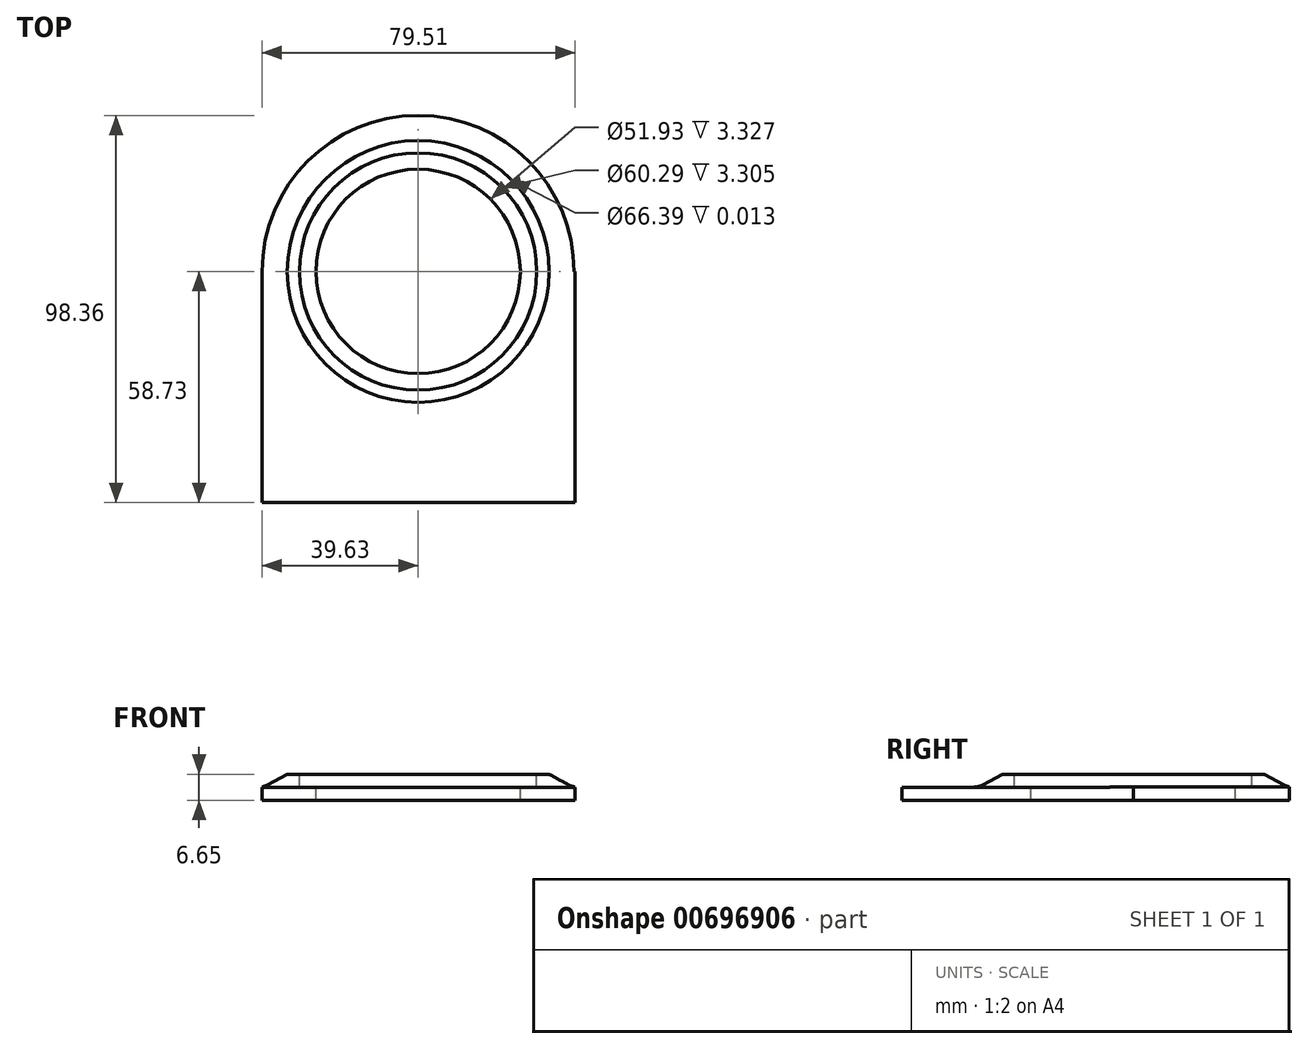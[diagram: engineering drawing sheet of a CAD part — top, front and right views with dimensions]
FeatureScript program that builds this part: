
annotation { "Feature Type Name" : "Feature", "Feature Type Description" : "" }
export const myFeature = defineFeature(function(context is Context, id is Id, definition is map)
    precondition{}
    {
        {
            var Q0;
            Q0=qCreatedBy(makeId("Top.planeOp"),FACE);
            var sketch = newSketch(context, id + "F0", { "sketchPlane" : qUnion([Q0])});
            skCircle(sketch, "E0", {"center": v(0, 0) * mm, "radius": 30.21 * mm});
            skCircle(sketch, "E1", {"center": v(0, 0) * mm, "radius": 26.11 * mm});
            skCircle(sketch, "E2", {"center": v(0, 0) * mm, "radius": 33.2 * mm});
            skCircle(sketch, "E3", {"center": v(0, 0) * mm, "radius": 39.63 * mm});
            skLineSegment(sketch, "E4.bottom", {"start": v(-39.63, 0) * mm, "end": v(39.88, 0) * mm});
            skLineSegment(sketch, "E4.top", {"start": v(-39.63, -58.73) * mm, "end": v(39.88, -58.73) * mm});
            skLineSegment(sketch, "E4.left", {"start": v(-39.63, 0) * mm, "end": v(-39.63, -58.73) * mm});
            skLineSegment(sketch, "E4.right", {"start": v(39.88, 0) * mm, "end": v(39.88, -58.73) * mm});
            skSolve(sketch);
        }
        {
            var Q0;
            Q0=qCreatedBy(makeId("Front.planeOp"),FACE);
            var sketch = newSketch(context, id + "F1", { "sketchPlane" : qUnion([Q0])});
            skLineSegment(sketch, "E5.bottom", {"start": v(39.37, -4.97) * mm, "end": v(-39.37, -4.97) * mm});
            skLineSegment(sketch, "E5.top", {"start": v(39.37, 4.97) * mm, "end": v(-39.37, 4.97) * mm});
            skLineSegment(sketch, "E5.left", {"start": v(39.37, -4.97) * mm, "end": v(39.37, 4.97) * mm});
            skLineSegment(sketch, "E5.right", {"start": v(-39.37, -4.97) * mm, "end": v(-39.37, 4.97) * mm});
            skPoint(sketch, "E5.middle", {"position": v(0, 0) * mm});
            skLineSegment(sketch, "E6.bottom", {"start": v(33.25, -4.97) * mm, "end": v(-33.25, -4.97) * mm});
            skLineSegment(sketch, "E6.top", {"start": v(33.25, 4.97) * mm, "end": v(-33.25, 4.97) * mm});
            skLineSegment(sketch, "E6.left", {"start": v(33.25, -4.97) * mm, "end": v(33.25, 4.97) * mm});
            skLineSegment(sketch, "E6.right", {"start": v(-33.25, -4.97) * mm, "end": v(-33.25, 4.97) * mm});
            skLineSegment(sketch, "E7.bottom", {"start": v(25.97, -4.97) * mm, "end": v(-25.97, -4.97) * mm});
            skLineSegment(sketch, "E7.top", {"start": v(25.97, 4.97) * mm, "end": v(-25.97, 4.97) * mm});
            skLineSegment(sketch, "E7.left", {"start": v(25.97, -4.97) * mm, "end": v(25.97, 4.97) * mm});
            skLineSegment(sketch, "E7.right", {"start": v(-25.97, -4.97) * mm, "end": v(-25.97, 4.97) * mm});
            skLineSegment(sketch, "E8.bottom", {"start": v(30.15, -4.97) * mm, "end": v(-30.15, -4.97) * mm});
            skLineSegment(sketch, "E8.top", {"start": v(30.15, 4.97) * mm, "end": v(-30.15, 4.97) * mm});
            skLineSegment(sketch, "E8.left", {"start": v(30.15, -4.97) * mm, "end": v(30.15, 4.97) * mm});
            skLineSegment(sketch, "E8.right", {"start": v(-30.15, -4.97) * mm, "end": v(-30.15, 4.97) * mm});
            skLineSegment(sketch, "E9.bottom", {"start": v(39.37, -1.66) * mm, "end": v(-39.37, -1.66) * mm});
            skLineSegment(sketch, "E9.top", {"start": v(39.37, 1.66) * mm, "end": v(-39.37, 1.66) * mm});
            skLineSegment(sketch, "E9.left", {"start": v(39.37, -1.66) * mm, "end": v(39.37, 1.66) * mm});
            skLineSegment(sketch, "E9.right", {"start": v(-39.37, -1.66) * mm, "end": v(-39.37, 1.66) * mm});
            skLineSegment(sketch, "E10", {"start": v(-39.37, 1.66) * mm, "end": v(-33.25, 4.97) * mm});
            skLineSegment(sketch, "E11", {"start": v(33.25, 4.97) * mm, "end": v(39.37, 1.66) * mm});
            skLineSegment(sketch, "E12", {"start": v(0, 4.97) * mm, "end": v(0, -4.97) * mm});
            skSolve(sketch);
        }
        {
            var Q0;
            {var subQ0=sQuery(id+"F1.wireOp",EDGE,"E10");Q0=makeQuery(id+"F1.imprint","IMPRINT",FACE,{"disambiguationData":[TD([[makeQuery(id+"F1.imprint","IMPRINT",EDGE,{"derivedFrom":subQ0}),-1.0]])]});}
            var Q1;
            {var subQ0=sQuery(id+"F1.wireOp",EDGE,"E6.right");var subQ5=sQuery(id+"F1.wireOp",EDGE,"E9.top");var subQ6=makeQuery(id+"F1.imprint","INTERSECT",VERTEX,{"derivedFrom":[subQ0,subQ5]});Q1=makeQuery(id+"F1.imprint","IMPRINT",FACE,{"disambiguationData":[TD([[makeQuery(id+"F1.imprint","IMPRINT",EDGE,{"disambiguationData":[TD([[subQ6,1.0]])],"derivedFrom":subQ5}),-1.0]])]});}
            var Q2;
            {var subQ0=sQuery(id+"F1.wireOp",EDGE,"E9.bottom");var subQ1=sQuery(id+"F1.wireOp",EDGE,"E7.right");var subQ2=makeQuery(id+"F1.imprint","INTERSECT",VERTEX,{"derivedFrom":[subQ1,subQ0]});Q2=makeQuery(id+"F1.imprint","IMPRINT",FACE,{"disambiguationData":[TD([[makeQuery(id+"F1.imprint","IMPRINT",EDGE,{"disambiguationData":[TD([[subQ2,-1.0]])],"derivedFrom":subQ1}),1.0]])]});}
            var Q3;
            {var subQ0=sQuery(id+"F1.wireOp",EDGE,"E9.bottom");var subQ1=sQuery(id+"F1.wireOp",EDGE,"E6.right");var subQ2=makeQuery(id+"F1.imprint","INTERSECT",VERTEX,{"derivedFrom":[subQ1,subQ0]});Q3=makeQuery(id+"F1.imprint","IMPRINT",FACE,{"disambiguationData":[TD([[makeQuery(id+"F1.imprint","IMPRINT",EDGE,{"disambiguationData":[TD([[subQ2,-1.0]])],"derivedFrom":subQ1}),-1.0]])]});}
            var Q4;
            {var subQ5=sQuery(id+"F1.wireOp",EDGE,"E9.right");Q4=makeQuery(id+"F1.imprint","IMPRINT",FACE,{"disambiguationData":[TD([[makeQuery(id+"F1.imprint","IMPRINT",EDGE,{"derivedFrom":subQ5}),-1.0]])]});}
            var Q5;
            Q5=sQuery(id+"F1.wireOp",EDGE,"E12");
            revolve(context, id + "F2", {"entities" : qUnion([Q0, Q1, Q2, Q3, Q4]), "axis" : qUnion([Q5]), "revolveType" : RevolveType.FULL});
        }
        {
            var Q0;
            Q0 = qSketchRegion(id + "F0", true);
            extrude(context, id + "F3", {"entities" : qUnion([Q0]), "operationType" : NewBodyOperationType.ADD, "endBound" : BoundingType.SYMMETRIC, "depth" : 3.35 * mm, "offsetDistance" : 25.4 * mm});
        }
        {
            var Q0;
            Q0=makeQuery(id+"F3.boolean.opBoolean","INTERSECT",EDGE,{"derivedFrom":[makeQuery(id+"F2.opRevolve","SWEPT_FACE",FACE,{"disambiguationData":[OSD([sQuery(id+"F1.wireOp",EDGE,"E10")])]}),makeQuery(id+"F3.opExtrude","CAP_FACE",FACE,{"disambiguationData":[OSD([sQuery(id+"F0.wireOp",EDGE,"E2"),sQuery(id+"F0.wireOp",EDGE,"E3"),sQuery(id+"F0.wireOp",EDGE,"E4.bottom"),sQuery(id+"F0.wireOp",EDGE,"E4.top"),sQuery(id+"F0.wireOp",EDGE,"E4.left"),sQuery(id+"F0.wireOp",EDGE,"E4.right")])],"isStart":false})]});
            fillet(context, id + "F4", {"entities" : qUnion([Q0]), "radius" : 5.08 * mm, "tangentPropagation" : true, "allowEdgeOverflow" : false});
        }
    });
